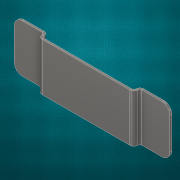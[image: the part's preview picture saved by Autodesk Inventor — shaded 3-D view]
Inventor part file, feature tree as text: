
AUTODESK INVENTOR PART (.ipt)
format: ipt  version: 2017 (Build 210142000, 142)  size: 171,008 bytes
history: native  units: in
note: dims shown in document units (in); Inventor stores cm internally (conversion verified against a paired STEP export)
features: sheet_metal_op x7, sketch x3, other x3, fillet x1
ambient origin geometry x8: Origin, YZ Plane, XZ Plane, XY Plane, X Axis, Y Axis, Z Axis, Center Point
bodies: Solid1 (feature_tree)
feature tree (14):
  sheet_metal_op  "Face1"
  sheet_metal_op  "Flange1"
  sheet_metal_op  "Flange2"
  fillet  "Fillet1"  Radius=3.0in
  sketch  "Sketch1"  dims[d1=1.5in]
  other  "Plate1"
  sketch  "Sketch2"  dims[d2=0.0625in]
  other  "Plate2"
  sheet_metal_op  "Bend1"
  sheet_metal_op  "Corner1"
  sketch  "Sketch3"  dims[d3=0.0625in d4=0.0312in d5=0.125in d6=0.0625in d7=0.19in d8=90.0deg d9=0.0625in d10=0.25in d11=0.0625in d12=0.0625in d13=0.0625in d14=0.0312in d15=0.125in d16=0.0625in d17=1.0in d18=90.0deg d19=0.0625in d20=0.25in d21=0.0625in d22=0.0625in d23=0.25in]
  other  "Plate3"
  sheet_metal_op  "Bend2"
  sheet_metal_op  "Corner2"
